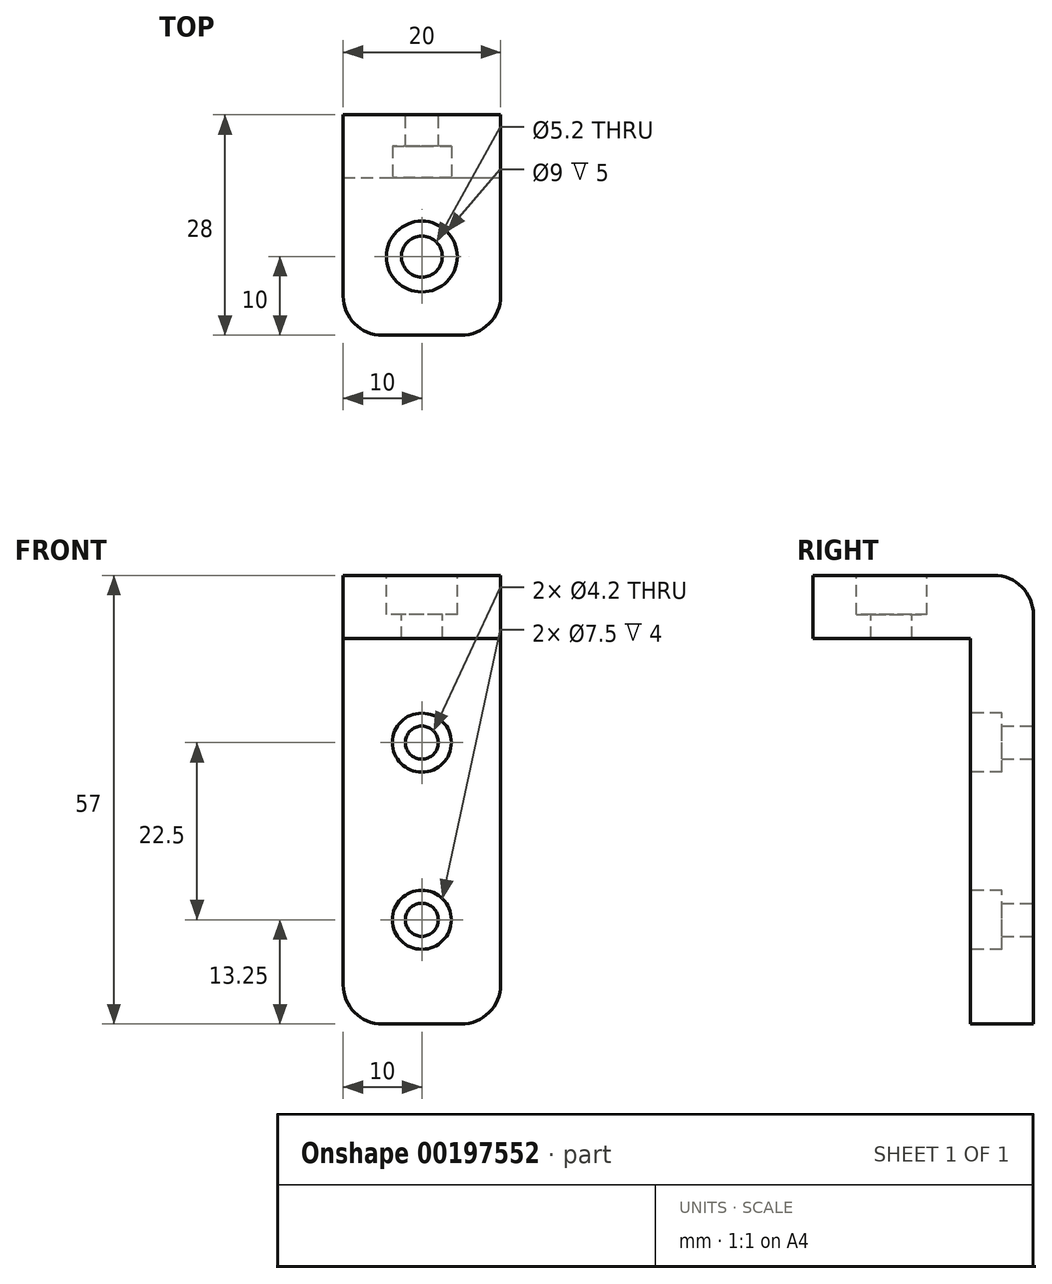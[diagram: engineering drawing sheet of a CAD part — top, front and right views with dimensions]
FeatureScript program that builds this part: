
annotation { "Feature Type Name" : "Feature", "Feature Type Description" : "" }
export const myFeature = defineFeature(function(context is Context, id is Id, definition is map)
    precondition{}
    {
        {
            var Q0;
            Q0=qCreatedBy(makeId("Front.planeOp"),FACE);
            var sketch = newSketch(context, id + "F0", { "sketchPlane" : qUnion([Q0])});
            skLineSegment(sketch, "E0.bottom", {"start": v(-10, 49) * mm, "end": v(10, 49) * mm});
            skLineSegment(sketch, "E0.top", {"start": v(-10, 0) * mm, "end": v(10, 0) * mm});
            skLineSegment(sketch, "E0.left", {"start": v(-10, 49) * mm, "end": v(-10, 0) * mm});
            skLineSegment(sketch, "E0.right", {"start": v(10, 49) * mm, "end": v(10, 0) * mm});
            skCircle(sketch, "E1", {"center": v(0, 35.75) * mm, "radius": 2.1 * mm});
            skPoint(sketch, "E1.centerSnap0", {"position": v(0, 49) * mm});
            skCircle(sketch, "E2", {"center": v(0, 13.25) * mm, "radius": 2.1 * mm});
            skSolve(sketch);
        }
        {
            var Q0;
            Q0=qSketchRegion(id+"F0",true);
            extrude(context, id + "F1", {"entities" : qUnion([Q0]), "depth" : 8 * mm});
        }
        {
            var Q0;
            Q0=makeQuery(id+"F1.opExtrude","CAP_FACE",FACE,{"disambiguationData":[OSD([sQuery(id+"F0.wireOp",EDGE,"E0.bottom"),sQuery(id+"F0.wireOp",EDGE,"E0.top"),sQuery(id+"F0.wireOp",EDGE,"E0.left"),sQuery(id+"F0.wireOp",EDGE,"E0.right"),sQuery(id+"F0.wireOp",EDGE,"E1"),sQuery(id+"F0.wireOp",EDGE,"E2")])],"isStart":false});
            var sketch = newSketch(context, id + "F2", { "sketchPlane" : qUnion([Q0])});
            skPoint(sketch, "E3", {"position": v(0, 35.75) * mm});
            skPoint(sketch, "E4", {"position": v(0, 13.25) * mm});
            skCircle(sketch, "E5", {"center": v(0, 35.75) * mm, "radius": 3.75 * mm});
            skCircle(sketch, "E6", {"center": v(0, 13.25) * mm, "radius": 3.75 * mm});
            skSolve(sketch);
        }
        {
            var Q0;
            Q0=qSketchRegion(id+"F2",true);
            extrude(context, id + "F3", {"entities" : qUnion([Q0]), "operationType" : NewBodyOperationType.REMOVE, "oppositeDirection" : true, "depth" : 4 * mm});
        }
        {
            var Q0;
            Q0=makeQuery(id+"F1.opExtrude","CAP_FACE",FACE,{"disambiguationData":[OSD([sQuery(id+"F0.wireOp",EDGE,"E0.bottom"),sQuery(id+"F0.wireOp",EDGE,"E0.top"),sQuery(id+"F0.wireOp",EDGE,"E0.left"),sQuery(id+"F0.wireOp",EDGE,"E0.right"),sQuery(id+"F0.wireOp",EDGE,"E1"),sQuery(id+"F0.wireOp",EDGE,"E2")])],"isStart":true});
            var sketch = newSketch(context, id + "F4", { "sketchPlane" : qUnion([Q0])});
            skLineSegment(sketch, "E7.bottom", {"start": v(-10, 49) * mm, "end": v(10, 49) * mm});
            skLineSegment(sketch, "E7.top", {"start": v(-10, 57) * mm, "end": v(10, 57) * mm});
            skLineSegment(sketch, "E7.left", {"start": v(-10, 49) * mm, "end": v(-10, 57) * mm});
            skLineSegment(sketch, "E7.right", {"start": v(10, 49) * mm, "end": v(10, 57) * mm});
            skSolve(sketch);
        }
        {
            var Q0;
            Q0=qSketchRegion(id+"F4",true);
            extrude(context, id + "F5", {"entities" : qUnion([Q0]), "operationType" : NewBodyOperationType.ADD, "oppositeDirection" : true, "depth" : 28 * mm});
        }
        {
            var Q0;
            Q0=makeQuery(id+"F5.opExtrude","SWEPT_FACE",FACE,{"disambiguationData":[OSD([sQuery(id+"F4.wireOp",EDGE,"E7.top")])]});
            var sketch = newSketch(context, id + "F6", { "sketchPlane" : qUnion([Q0])});
            skCircle(sketch, "E8", {"center": v(0, -18) * mm, "radius": 2.6 * mm});
            skPoint(sketch, "E8.centerSnap0", {"position": v(0, -28) * mm});
            skSolve(sketch);
        }
        {
            var Q0;
            Q0=qSketchRegion(id+"F6",true);
            extrude(context, id + "F7", {"entities" : qUnion([Q0]), "operationType" : NewBodyOperationType.REMOVE, "endBound" : BoundingType.THROUGH_ALL, "oppositeDirection" : true, "depth" : 25 * mm});
        }
        {
            var Q0;
            Q0=makeQuery(id+"F5.opExtrude","SWEPT_FACE",FACE,{"disambiguationData":[OSD([sQuery(id+"F4.wireOp",EDGE,"E7.top")])]});
            var sketch = newSketch(context, id + "F8", { "sketchPlane" : qUnion([Q0])});
            skPoint(sketch, "E9", {"position": v(0, -18) * mm});
            skCircle(sketch, "E10", {"center": v(0, -18) * mm, "radius": 4.5 * mm});
            skSolve(sketch);
        }
        {
            var Q0;
            Q0=qSketchRegion(id+"F8",true);
            extrude(context, id + "F9", {"entities" : qUnion([Q0]), "operationType" : NewBodyOperationType.REMOVE, "oppositeDirection" : true, "depth" : 5 * mm});
        }
        {
            var Q0;
            Q0=makeQuery(id+"F5.opExtrude","CAP_EDGE",EDGE,{"disambiguationData":[OSD([sQuery(id+"F4.wireOp",EDGE,"E7.left")])],"isStart":false});
            var Q1;
            Q1=makeQuery(id+"F5.opExtrude","CAP_EDGE",EDGE,{"disambiguationData":[OSD([sQuery(id+"F4.wireOp",EDGE,"E7.right")])],"isStart":false});
            var Q2;
            Q2=makeQuery(id+"F5.opExtrude","CAP_EDGE",EDGE,{"disambiguationData":[OSD([sQuery(id+"F4.wireOp",EDGE,"E7.top")])],"isStart":true});
            var Q3;
            Q3=makeQuery(id+"F1.opExtrude","SWEPT_EDGE",EDGE,{"disambiguationData":[OSD([sQuery(id+"F0.wireOp",EDGE,"E0.top"),sQuery(id+"F0.wireOp",EDGE,"E0.right")])]});
            var Q4;
            Q4=makeQuery(id+"F1.opExtrude","SWEPT_EDGE",EDGE,{"disambiguationData":[OSD([sQuery(id+"F0.wireOp",EDGE,"E0.top"),sQuery(id+"F0.wireOp",EDGE,"E0.left")])]});
            fillet(context, id + "F10", {"entities" : qUnion([Q0, Q1, Q2, Q3, Q4]), "radius" : 5 * mm, "tangentPropagation" : true, "allowEdgeOverflow" : false});
        }
    });
